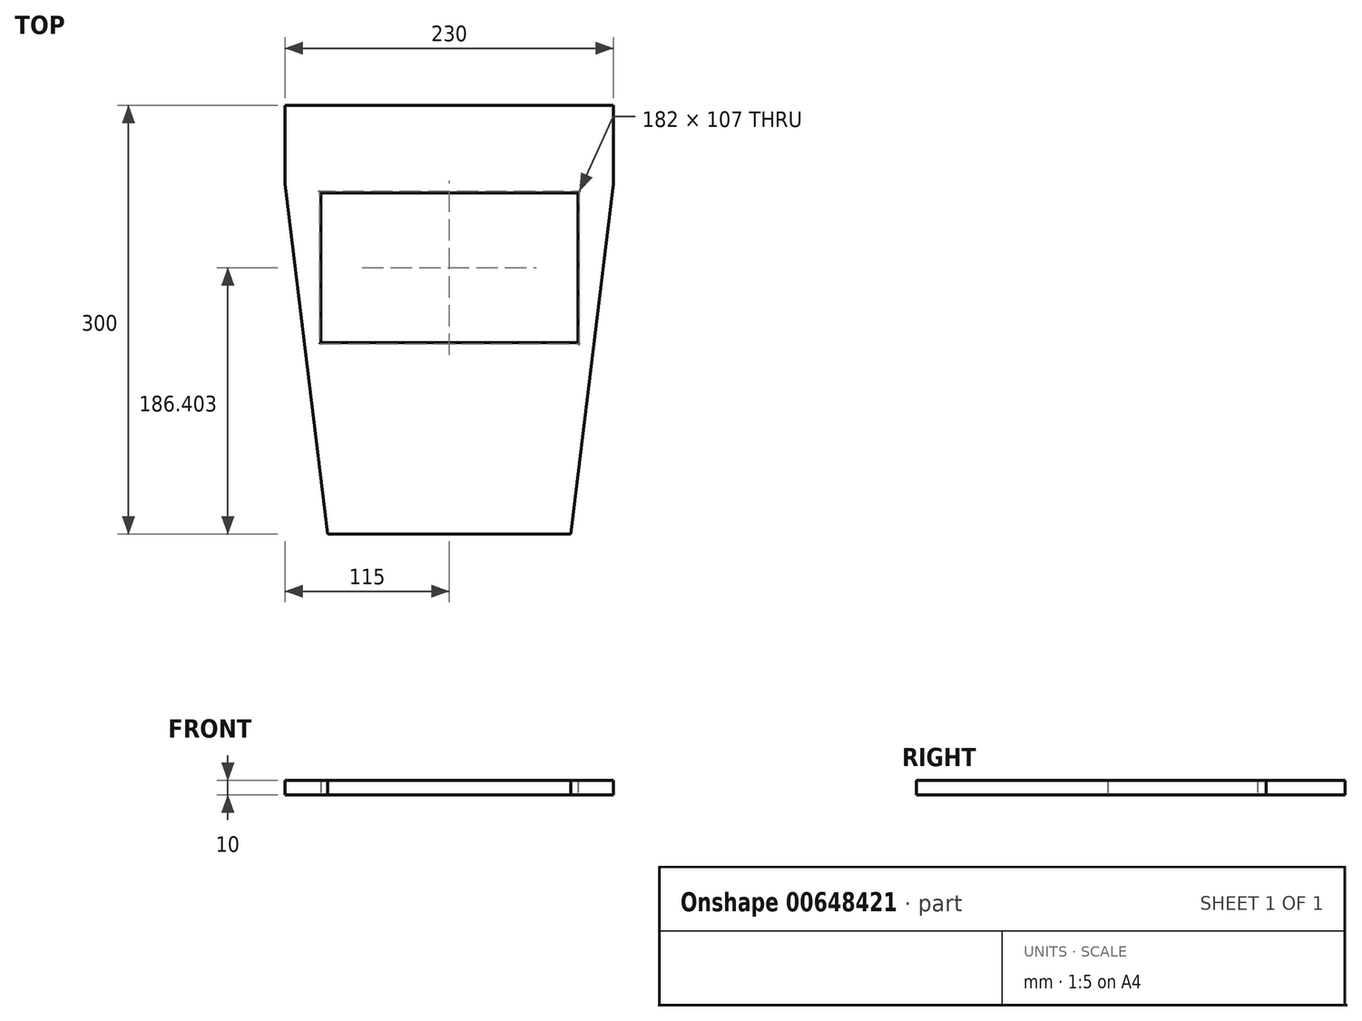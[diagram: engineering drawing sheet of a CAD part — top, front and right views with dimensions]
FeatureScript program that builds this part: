
annotation { "Feature Type Name" : "Feature", "Feature Type Description" : "" }
export const myFeature = defineFeature(function(context is Context, id is Id, definition is map)
    precondition{}
    {
        {
            var Q0;
            Q0=qCreatedBy(makeId("Top.planeOp"),FACE);
            var sketch = newSketch(context, id + "F0", { "sketchPlane" : qUnion([Q0])});
            skLineSegment(sketch, "E0.bottom", {"start": v(115, 115.05) * mm, "end": v(-115, 115.05) * mm});
            skLineSegment(sketch, "E0.top", {"start": v(115, 170.05) * mm, "end": v(-115, 170.05) * mm});
            skLineSegment(sketch, "E0.left", {"start": v(115, 115.05) * mm, "end": v(115, 170.05) * mm});
            skLineSegment(sketch, "E0.right", {"start": v(-115, 115.05) * mm, "end": v(-115, 170.05) * mm});
            skPoint(sketch, "E0.middle", {"position": v(0, 142.55) * mm});
            skLineSegment(sketch, "E1.bottom", {"start": v(85, -129.95) * mm, "end": v(-85, -129.95) * mm});
            skLineSegment(sketch, "E1.top", {"start": v(85, -109.95) * mm, "end": v(-85, -109.95) * mm});
            skLineSegment(sketch, "E1.left", {"start": v(85, -129.95) * mm, "end": v(85, -109.95) * mm});
            skLineSegment(sketch, "E1.right", {"start": v(-85, -129.95) * mm, "end": v(-85, -109.95) * mm});
            skPoint(sketch, "E1.middle", {"position": v(0, -119.95) * mm});
            skLineSegment(sketch, "E2", {"start": v(115, 115.05) * mm, "end": v(85, -129.95) * mm});
            skLineSegment(sketch, "E3", {"start": v(-115, 115.05) * mm, "end": v(-85, -129.95) * mm});
            skLineSegment(sketch, "E4.bottom", {"start": v(90, 108.95) * mm, "end": v(-90, 108.95) * mm});
            skLineSegment(sketch, "E4.top", {"start": v(90, 3.95) * mm, "end": v(-90, 3.95) * mm});
            skLineSegment(sketch, "E4.left", {"start": v(90, 108.95) * mm, "end": v(90, 3.95) * mm});
            skLineSegment(sketch, "E4.right", {"start": v(-90, 108.95) * mm, "end": v(-90, 3.95) * mm});
            skPoint(sketch, "E4.middle", {"position": v(0, 56.45) * mm});
            skSolve(sketch);
        }
        {
            var Q0;
            Q0 = qSketchRegion(id + "F0", true);
            extrude(context, id + "F1", {"entities" : qUnion([Q0]), "depth" : 10 * mm, "offsetDistance" : 25 * mm});
        }
        {
            var Q0;
            Q0=makeQuery(id+"F1.opExtrude","CAP_EDGE",EDGE,{"disambiguationData":[OSD([sQuery(id+"F0.wireOp",EDGE,"E4.bottom")])],"isStart":true});
            var Q1;
            Q1=makeQuery(id+"F1.opExtrude","CAP_EDGE",EDGE,{"disambiguationData":[OSD([sQuery(id+"F0.wireOp",EDGE,"E4.left")])],"isStart":false});
            var Q2;
            Q2=makeQuery(id+"F1.opExtrude","CAP_EDGE",EDGE,{"disambiguationData":[OSD([sQuery(id+"F0.wireOp",EDGE,"E4.top")])],"isStart":false});
            var Q3;
            Q3=makeQuery(id+"F1.opExtrude","CAP_EDGE",EDGE,{"disambiguationData":[OSD([sQuery(id+"F0.wireOp",EDGE,"E4.right")])],"isStart":false});
            var Q4;
            Q4=makeQuery(id+"F1.opExtrude","CAP_EDGE",EDGE,{"disambiguationData":[OSD([sQuery(id+"F0.wireOp",EDGE,"E4.top")])],"isStart":true});
            var Q5;
            Q5=makeQuery(id+"F1.opExtrude","CAP_EDGE",EDGE,{"disambiguationData":[OSD([sQuery(id+"F0.wireOp",EDGE,"E4.right")])],"isStart":true});
            var Q6;
            Q6=makeQuery(id+"F1.opExtrude","CAP_EDGE",EDGE,{"disambiguationData":[OSD([sQuery(id+"F0.wireOp",EDGE,"E4.bottom")])],"isStart":false});
            var Q7;
            Q7=makeQuery(id+"F1.opExtrude","CAP_EDGE",EDGE,{"disambiguationData":[OSD([sQuery(id+"F0.wireOp",EDGE,"E4.left")])],"isStart":true});
            fillet(context, id + "F2", {"entities" : qUnion([Q0, Q1, Q2, Q3, Q4, Q5, Q6, Q7]), "radius" : 1 * mm, "tangentPropagation" : true, "allowEdgeOverflow" : false});
        }
    });
